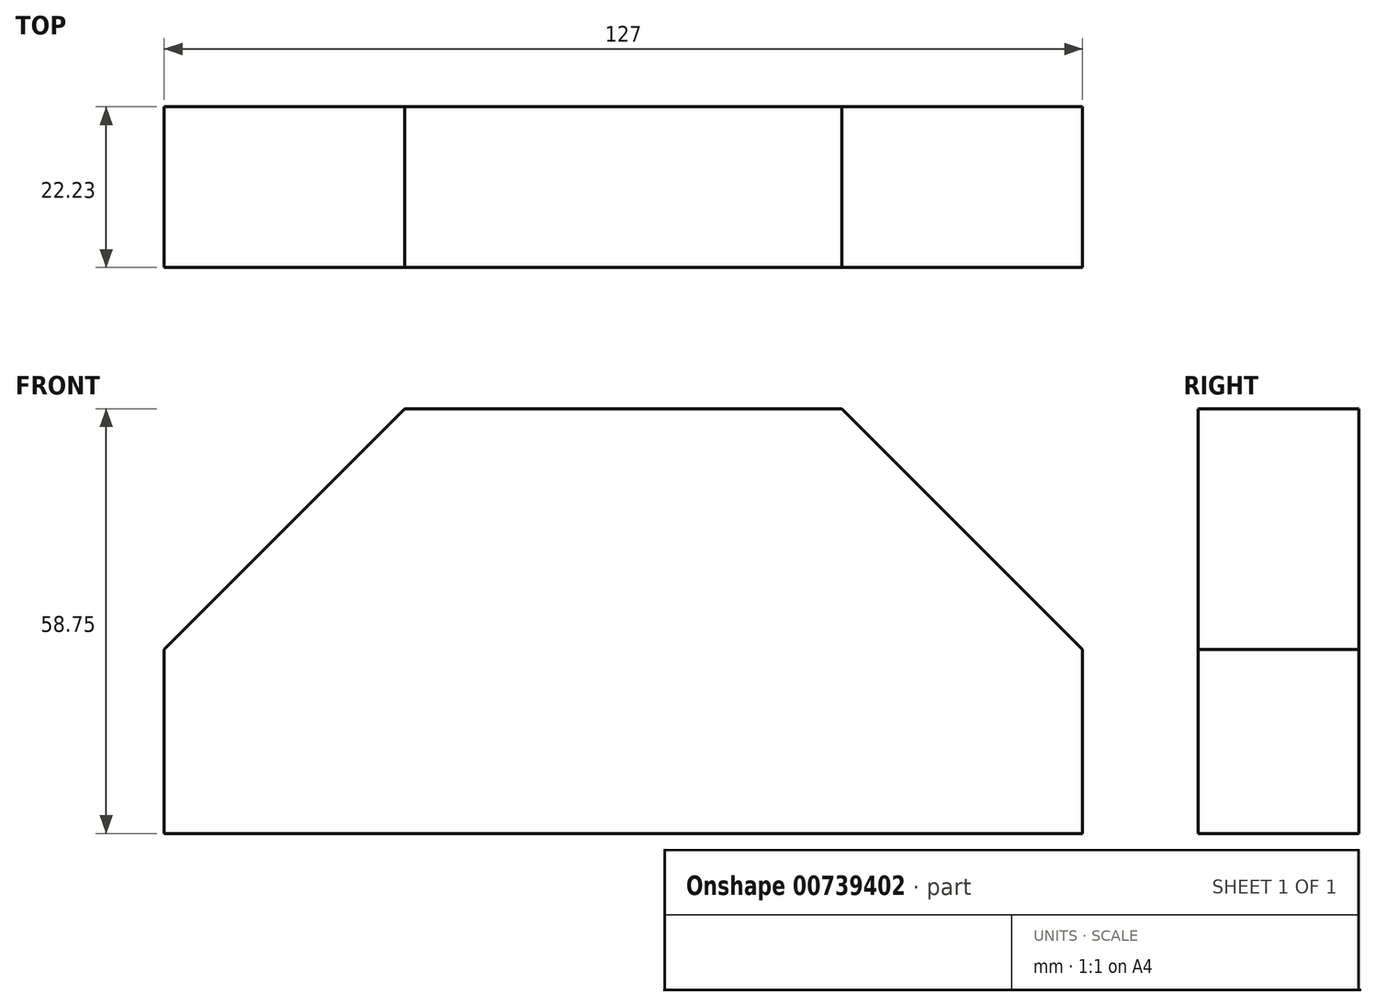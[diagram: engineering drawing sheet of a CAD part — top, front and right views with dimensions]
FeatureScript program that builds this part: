
annotation { "Feature Type Name" : "Feature", "Feature Type Description" : "" }
export const myFeature = defineFeature(function(context is Context, id is Id, definition is map)
    precondition{}
    {
        {
            var Q0;
            Q0=qCreatedBy(makeId("Front.planeOp"),FACE);
            var sketch = newSketch(context, id + "F0", { "sketchPlane" : qUnion([Q0])});
            skLineSegment(sketch, "E0", {"start": v(0, 0) * mm, "end": v(-127, 0) * mm});
            skLineSegment(sketch, "E1", {"start": v(-127, 0) * mm, "end": v(-127, 25.48) * mm});
            skLineSegment(sketch, "E2", {"start": v(-127, 25.48) * mm, "end": v(-93.73, 58.75) * mm});
            skLineSegment(sketch, "E3", {"start": v(-93.73, 58.75) * mm, "end": v(-33.27, 58.75) * mm});
            skLineSegment(sketch, "E4", {"start": v(-33.27, 58.75) * mm, "end": v(0, 25.48) * mm});
            skLineSegment(sketch, "E5", {"start": v(0, 25.48) * mm, "end": v(0, 0) * mm});
            skSolve(sketch);
        }
        {
            var Q0;
            Q0=makeQuery(id+"F0.imprint","IMPRINT",FACE,{"disambiguationData":[TD([[makeQuery(id+"F0.imprint","IMPRINT",EDGE,{"derivedFrom":sQuery(id+"F0.wireOp",EDGE,"E0")}),-1.0]])]});
            extrude(context, id + "F1", {"entities" : qUnion([Q0]), "depth" : 22.22 * mm, "offsetDistance" : 25.4 * mm});
        }
    });
